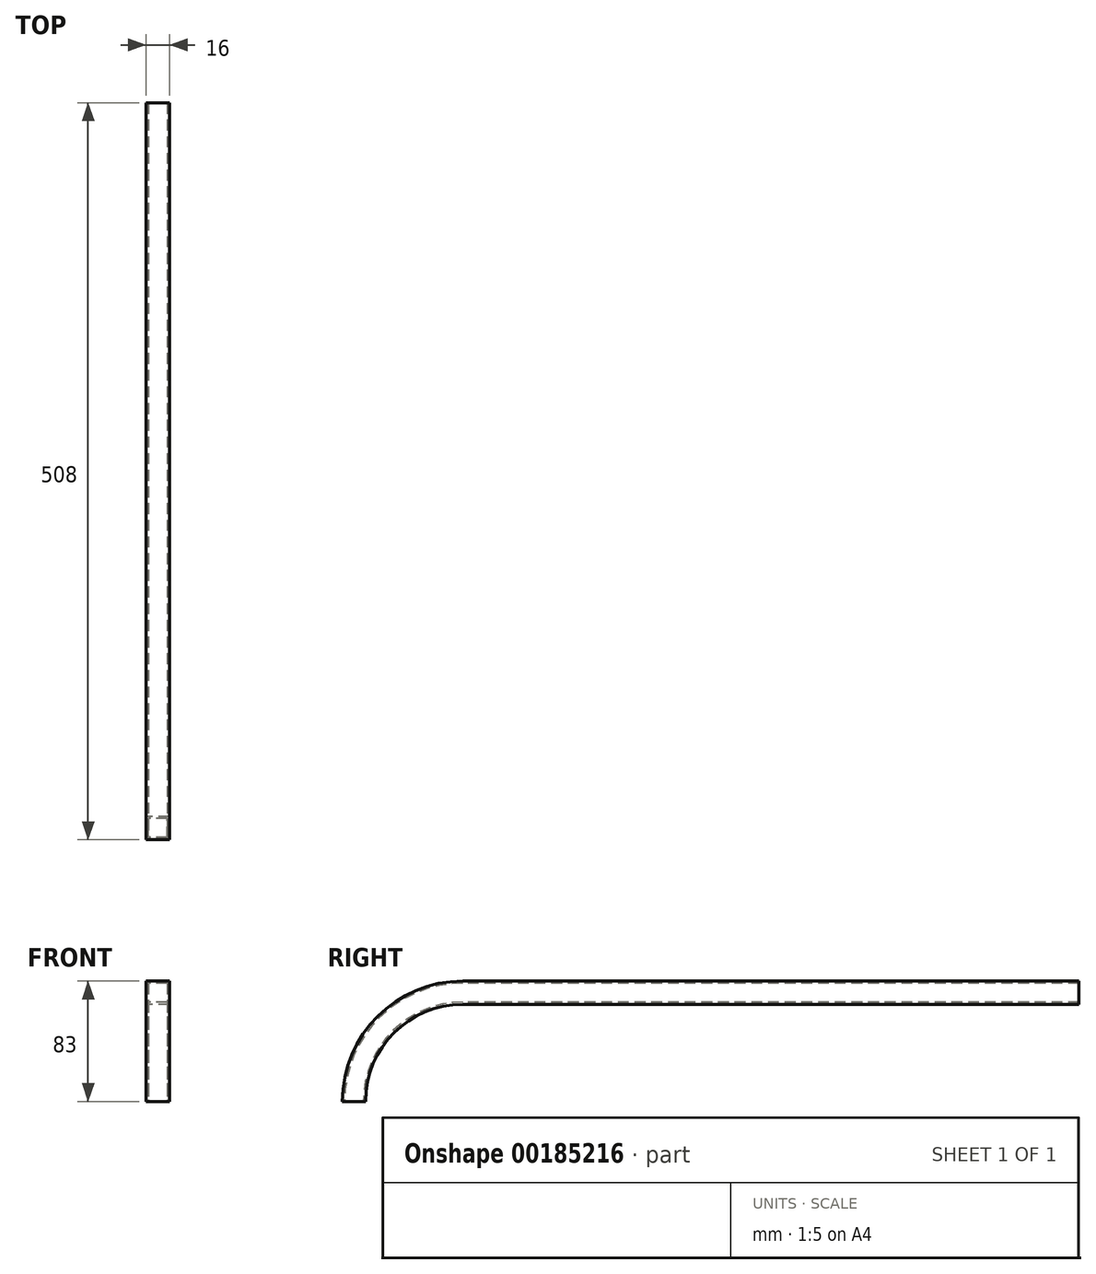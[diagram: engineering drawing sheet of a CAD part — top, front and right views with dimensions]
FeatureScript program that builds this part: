
annotation { "Feature Type Name" : "Feature", "Feature Type Description" : "" }
export const myFeature = defineFeature(function(context is Context, id is Id, definition is map)
    precondition{}
    {
        {
            var Q0;
            Q0=qCreatedBy(makeId("Front.planeOp"),FACE);
            var sketch = newSketch(context, id + "F0", { "sketchPlane" : qUnion([Q0])});
            skLineSegment(sketch, "E0.bottom", {"start": v(8, 8) * mm, "end": v(-8, 8) * mm});
            skLineSegment(sketch, "E0.top", {"start": v(8, -8) * mm, "end": v(-8, -8) * mm});
            skLineSegment(sketch, "E0.left", {"start": v(8, 8) * mm, "end": v(8, -8) * mm});
            skLineSegment(sketch, "E0.right", {"start": v(-8, 8) * mm, "end": v(-8, -8) * mm});
            skPoint(sketch, "E0.middle", {"position": v(0, 0) * mm});
            skLineSegment(sketch, "E1.0", {"start": v(6.5, 6.5) * mm, "end": v(-6.5, 6.5) * mm});
            skLineSegment(sketch, "E2.0", {"start": v(6.5, 6.5) * mm, "end": v(6.5, -6.5) * mm});
            skLineSegment(sketch, "E3.0", {"start": v(6.5, -6.5) * mm, "end": v(-6.5, -6.5) * mm});
            skLineSegment(sketch, "E4.0", {"start": v(-6.5, 6.5) * mm, "end": v(-6.5, -6.5) * mm});
            skSolve(sketch);
        }
        {
            var Q0;
            Q0=qCreatedBy(makeId("Right.planeOp"),FACE);
            var sketch = newSketch(context, id + "F1", { "sketchPlane" : qUnion([Q0])});
            skLineSegment(sketch, "E5", {"start": v(0, 0) * mm, "end": v(-425, 0) * mm});
            skArc(sketch, "E6", {"start": v(-425, 0) * mm, "mid": v(-478.03, -21.97) * mm, "end": v(-500, -75) * mm});
            skSolve(sketch);
        }
        {
            var Q0;
            Q0=makeQuery(id+"F0.imprint","IMPRINT",FACE,{"disambiguationData":[TD([[makeQuery(id+"F0.imprint","IMPRINT",EDGE,{"derivedFrom":sQuery(id+"F0.wireOp",EDGE,"E0.bottom")}),1.0]])]});
            var Q1;
            Q1=sQuery(id+"F1.wireOp",EDGE,"E5");
            var Q2;
            Q2=sQuery(id+"F1.wireOp",EDGE,"E6");
            sweep(context, id + "F2", {"profiles" : qUnion([Q0]), "path" : qUnion([Q1, Q2])});
        }
    });
